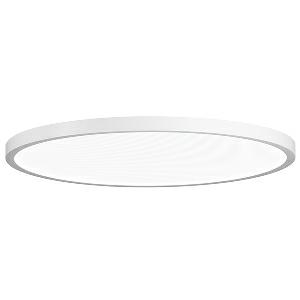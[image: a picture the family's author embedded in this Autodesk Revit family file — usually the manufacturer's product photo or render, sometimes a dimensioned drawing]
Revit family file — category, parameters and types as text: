
# Revit family: vivaa_fit_-_via_10000_940_d_00813146_5c67
name_source: partatom
category: Lighting Fixtures
units: mm (PartAtom-declared; Revit-internal decimal feet)

## family parameters
Cut with Voids When Loaded = No
Host = Face
Light Source = No
Part Type = Normal
Room Calculation Point = No
Round Connector Dimension = Use Diameter
Shared = No

## types (1)
- VIVAA.fit - VIA 10000/940/D (1 x LED, 10200 lm, 4000K)
    Apparent Load = 85 VA
    Approval mark = CE
    CIE Flux Codes = 66 90 98 49 100
    Color Rendering = 90-100
    Color Temperature = 4000K
    Control Gear = Electronic ballast
    Default Elevation = 1800 mm
    Description = VIA 10000/940/D|Surface-mounted luminaire.|light source:   Cold white   |work equipment: Power supply unit|luminous flux: 10200 lm|light distribution: Direct/indirect|class of protection: I|mains lead: Direct power supply 5 pin|glare control: optical film|special features: DALI Load 2x, Suitable as emergency lighting, Separated, direct and indirect light individually adjustable|
    Frequency = 50 Hz, 60 Hz
    Height = 48 mm  [stored 0.15748 ft]
    Lamp = 1 x LED
    Lamp Light Flux = 10200 lm
    Lamp count = 1
    Length = 600 mm
    Luminous efficacy = 120 lm/W
    Manufacturer = Waldmann
    ModVariant = No
    Model = 00813146
    Mounting Place = Ceiling
    Mounting Type = Surface mounted
    Number of Poles = 1
    OnlyDefault = Yes
    Power Factor = 1
    Product Name = VIVAA.fit - VIA 10000/940/D
    Product group = Ceiling mounted luminaire
    ProductGroupID = 3
    Protection Class = Protection class I
    Protection Degree = Degree of protection
    RLX_Detail_Level = 1
    RLX_Emergency_Light_Flux = 0 lm
    RLX_Emergency_Type = 0
    RLX_Emergency_Type_DB = No
    RlxData = <blob elided: 25773 chars, md5=4f310024>
    Socket = socket
    Standby Power = 0 W
    System Light Flux = 10200 lm
    System Power = 85 W
    Type Comments = Product without accessories
    Type Image = vivaa_2.0_anbau_600mm.jpg
    URL = http://relux.com
    VarID = ---
    Voltage = 230 V
    Voltage Range = 220-240 V
    Weight = 0.00 kg
    Width = 0 mm  [stored 0 ft]

note: [stored X ft] marks values corroborated as IEEE doubles in the binary element streams (Revit-internal decimal feet)

## geometry (parser evidence)
native form markers: Blend x4, Sweep x12
no freeform markers — native parametric forms only
